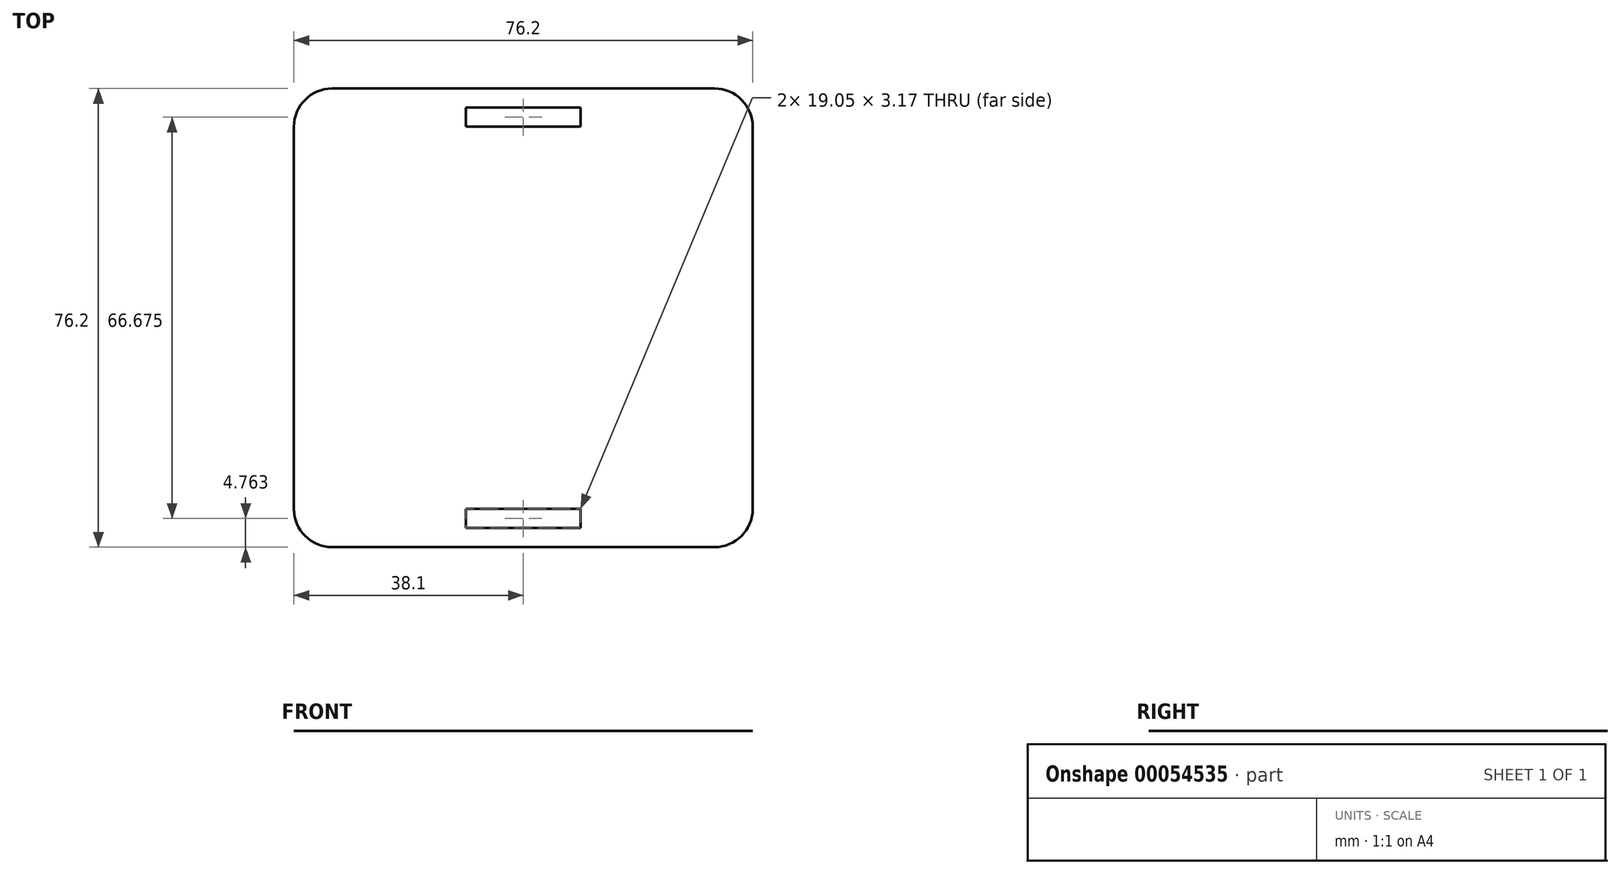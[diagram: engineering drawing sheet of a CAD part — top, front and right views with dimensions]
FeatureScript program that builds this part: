
annotation { "Feature Type Name" : "Feature", "Feature Type Description" : "" }
export const myFeature = defineFeature(function(context is Context, id is Id, definition is map)
    precondition{}
    {
        {
            var Q0;
            Q0=qCreatedBy(makeId("Top.planeOp"),FACE);
            var sketch = newSketch(context, id + "F0", { "sketchPlane" : qUnion([Q0])});
            skLineSegment(sketch, "E0.rect.bottom", {"start": v(-31.75, 38.1) * mm, "end": v(31.75, 38.1) * mm});
            skLineSegment(sketch, "E0.rect.top", {"start": v(-31.75, -38.1) * mm, "end": v(31.75, -38.1) * mm});
            skLineSegment(sketch, "E0.rect.left", {"start": v(-38.1, 31.75) * mm, "end": v(-38.1, -31.75) * mm});
            skLineSegment(sketch, "E0.rect.right", {"start": v(38.1, 31.75) * mm, "end": v(38.1, -31.75) * mm});
            skPoint(sketch, "E0.rect.middle", {"position": v(0, 0) * mm});
            skPoint(sketch, "E1.visualSharp", {"position": v(-38.1, 38.1) * mm});
            skArc(sketch, "E1.filletArc", {"start": v(-31.75, 38.1) * mm, "mid": v(-36.24, 36.24) * mm, "end": v(-38.1, 31.75) * mm});
            skPoint(sketch, "E2.visualSharp", {"position": v(38.1, 38.1) * mm});
            skArc(sketch, "E2.filletArc", {"start": v(38.1, 31.75) * mm, "mid": v(36.24, 36.24) * mm, "end": v(31.75, 38.1) * mm});
            skPoint(sketch, "E3.visualSharp", {"position": v(38.1, -38.1) * mm});
            skArc(sketch, "E3.filletArc", {"start": v(31.75, -38.1) * mm, "mid": v(36.24, -36.24) * mm, "end": v(38.1, -31.75) * mm});
            skPoint(sketch, "E4.visualSharp", {"position": v(-38.1, -38.1) * mm});
            skArc(sketch, "E4.filletArc", {"start": v(-38.1, -31.75) * mm, "mid": v(-36.24, -36.24) * mm, "end": v(-31.75, -38.1) * mm});
            skLineSegment(sketch, "E5.rect.bottom", {"start": v(-9.53, 31.75) * mm, "end": v(9.52, 31.75) * mm});
            skLineSegment(sketch, "E5.rect.top", {"start": v(-9.53, 34.93) * mm, "end": v(9.52, 34.93) * mm});
            skLineSegment(sketch, "E5.rect.left", {"start": v(-9.53, 31.75) * mm, "end": v(-9.53, 34.93) * mm});
            skLineSegment(sketch, "E5.rect.right", {"start": v(9.52, 31.75) * mm, "end": v(9.52, 34.93) * mm});
            skLineSegment(sketch, "E6.MirrorCS", {"start": v(-9.53, -31.75) * mm, "end": v(9.52, -31.75) * mm});
            skLineSegment(sketch, "E7.MirrorCS", {"start": v(-9.53, -34.93) * mm, "end": v(9.52, -34.93) * mm});
            skLineSegment(sketch, "E8", {"start": v(-9.53, -31.75) * mm, "end": v(-9.53, -34.93) * mm});
            skLineSegment(sketch, "E9", {"start": v(9.52, -31.75) * mm, "end": v(9.52, -34.93) * mm});
            skPoint(sketch, "E10", {"position": v(0, 36.51) * mm});
            skPoint(sketch, "E11.MirrorP", {"position": v(0, -36.51) * mm});
            skSolve(sketch);
        }
        {
            var Q0;
            Q0=makeQuery(id+"F0.imprint","IMPRINT",FACE,{"disambiguationData":[TD([[makeQuery(id+"F0.imprint","IMPRINT",EDGE,{"derivedFrom":sQuery(id+"F0.wireOp",EDGE,"E0.rect.bottom")}),-1.0]])]});
            extrude(context, id + "F1", {"entities" : qUnion([Q0]), "oppositeDirection" : true, "depth" : 1 / 203.2 * mm});
        }
    });
